# Revit family: Edelstahlrohrschelle V2A, M10, Ø 48-117
name_source: partatom
category: HLS-Bauteile
revit_build: Autodesk Revit 2017 (Build: 20190507_1515(x64)
units: mm (PartAtom-declared; Revit-internal decimal feet)

## family parameters
Arbeitsebenenbasiert = Ja
Beim Laden mit Abzugskörper schneiden = Nein
Bemaßung runder Anschluss = Durchmesser verwenden
Gemeinsam genutzt = Ja
Immer vertikal = Nein
Raumberechnungspunkt = Nein
Teiletyp = Normal

## types (9) — shared parameters
A = 10 mm  [stored 0.0328084 ft]
Anschluss = M10
Anschlußhöhe = 10 mm
Bauart = zweiteilig
DF1 = 13 mm
DF2 = 16 mm  [stored 0.0524934 ft]
DVS = 7 mm  [stored 0.0229659 ft]
Fabrikat = MEFA
Firma = MEFA Befestigungs- und Montagesysteme GmbH
HGA = 8 mm  [stored 0.0262467 ft]
Kurztext1 = Rohrschelle Edelstahl V2A 20x2,0
MB = 20 mm  [stored 0.0656168 ft]
MD = 2 mm  [stored 0.00656168 ft]
Material = Edelstahl
Materialmaße = 20x2,0 mm
Mengeneinheit = St
Verschluss = Schraubenverschluss
Verschluss-Schraube = M6
Vorgabe-Ansicht = 1219 mm
max. zul. Last horizontal = 0.00 kN
max. zul. Last vertikal = 0.00 kN
vpe = 50 St
zero-valued in all types: Nennweite DN Rohr, Rohraußendurchmesser, Stärke Material

## per-type parameters (varying)
| type | AB | Achsabstand | Artikelnummer | B | D | Dmax | Dmin | EAN | Gewicht | Gewicht pro Bauteil | H | Kurztext2 | R | RM | Rohraußendurchmesser Zoll | S | max. Rohraußendurchmesser | min. Rohraußendurchmesser |
| Edelstahlrohrschelle V2A, M10, Ø 48- 55 | 7 mm  [stored 0.0229659 ft] | 74 mm | 0469210 | 88 mm | 55 mm  [stored 0.180446 ft] | 55 mm  [stored 0.180446 ft] | 48 mm  [stored 0.15748 ft] | 4250928412225 | 0.10 kg | 0.10 kg | 67 mm | 48 - 55 mm M10 | 28 mm | 30 mm | 1 1/2 Zoll | 75 mm | 55 mm  [stored 0.180446 ft] | 48 mm  [stored 0.15748 ft] |
| Edelstahlrohrschelle V2A, M10, Ø 57- 62 | 5 mm  [stored 0.0164042 ft] | 82 mm | 0469212 | 95 mm | 62 mm  [stored 0.203412 ft] | 62 mm  [stored 0.203412 ft] | 57 mm  [stored 0.187008 ft] | 4250928412249 | 0.10 kg | 0.10 kg | 74 mm  [stored 0.242782 ft] | 57 - 62 mm M10 | 31 mm  [stored 0.101706 ft] | 33 mm  [stored 0.108268 ft] | Zoll | 82 mm  [stored 0.269029 ft] | 62 mm  [stored 0.203412 ft] | 57 mm  [stored 0.187008 ft] |
| Edelstahlrohrschelle V2A, M10, Ø 63- 67 | 4 mm  [stored 0.0131234 ft] | 88 mm | 0469211 | 100 mm | 67 mm | 67 mm | 63 mm  [stored 0.206693 ft] | 4250928412232 | 0.11 kg | 0.11 kg | 79 mm | 63 - 67 mm M10 | 34 mm | 36 mm | 2 Zoll | 87 mm | 67 mm | 63 mm  [stored 0.206693 ft] |
| Edelstahlrohrschelle V2A, M10, Ø 68- 74 | 6 mm  [stored 0.019685 ft] | 94 mm | 0469213 | 107 mm | 74 mm  [stored 0.242782 ft] | 74 mm  [stored 0.242782 ft] | 68 mm | 4250928412256 | 0.12 kg | 0.12 kg | 86 mm  [stored 0.282152 ft] | 68 - 74 mm M10 | 37 mm  [stored 0.121391 ft] | 39 mm  [stored 0.127953 ft] | Zoll | 94 mm | 74 mm  [stored 0.242782 ft] | 68 mm |
| Edelstahlrohrschelle V2A, M10, Ø 75- 80 | 5 mm  [stored 0.0164042 ft] | 101 mm | 0469214 | 113 mm | 80 mm  [stored 0.262467 ft] | 80 mm  [stored 0.262467 ft] | 75 mm | 4250928412263 | 0.12 kg | 0.12 kg | 92 mm | 75 - 80 mm M10 | 40 mm  [stored 0.131234 ft] | 42 mm  [stored 0.137795 ft] | 2 1/2 Zoll | 100 mm | 80 mm  [stored 0.262467 ft] | 75 mm |
| Edelstahlrohrschelle V2A, M10, Ø 82- 90 | 8 mm  [stored 0.0262467 ft] | 110 mm | 0469215 | 123 mm | 90 mm | 90 mm | 82 mm  [stored 0.269029 ft] | 4250928412270 | 0.13 kg | 0.13 kg | 102 mm | 82 - 90 mm M10 | 45 mm  [stored 0.147638 ft] | 47 mm  [stored 0.154199 ft] | 3 Zoll | 110 mm | 90 mm | 82 mm  [stored 0.269029 ft] |
| Edelstahlrohrschelle V2A, M10, Ø 92-100 | 8 mm  [stored 0.0262467 ft] | 120 mm | 0469216 | 133 mm | 100 mm | 100 mm | 92 mm | 4250928412287 | 0.14 kg | 0.14 kg | 112 mm | 92 - 100 mm M10 | 50 mm  [stored 0.164042 ft] | 52 mm | Zoll | 120 mm | 100 mm | 92 mm |
| Edelstahlrohrschelle V2A, M10, Ø103-110 | 7 mm  [stored 0.0229659 ft] | 131 mm | 0469217 | 143 mm | 110 mm | 110 mm | 103 mm | 4250928412294 | 0.14 kg | 0.14 kg | 122 mm | 103 - 110 mm M10 | 55 mm  [stored 0.180446 ft] | 57 mm  [stored 0.187008 ft] | Zoll | 130 mm | 110 mm | 103 mm |
| Edelstahlrohrschelle V2A, M10, Ø112-117 | 5 mm  [stored 0.0164042 ft] | 138 mm | 0469218 | 150 mm | 117 mm | 117 mm | 112 mm | 4250928412300 | 0.15 kg | 0.15 kg | 129 mm | 112 - 117 mm M10 | 59 mm  [stored 0.19357 ft] | 61 mm | 4 Zoll | 137 mm | 117 mm | 112 mm |

note: [stored X ft] marks values corroborated as IEEE doubles in the binary element streams (Revit-internal decimal feet)

## geometry (parser evidence)
native form markers: Sweep x5
no freeform markers — native parametric forms only
